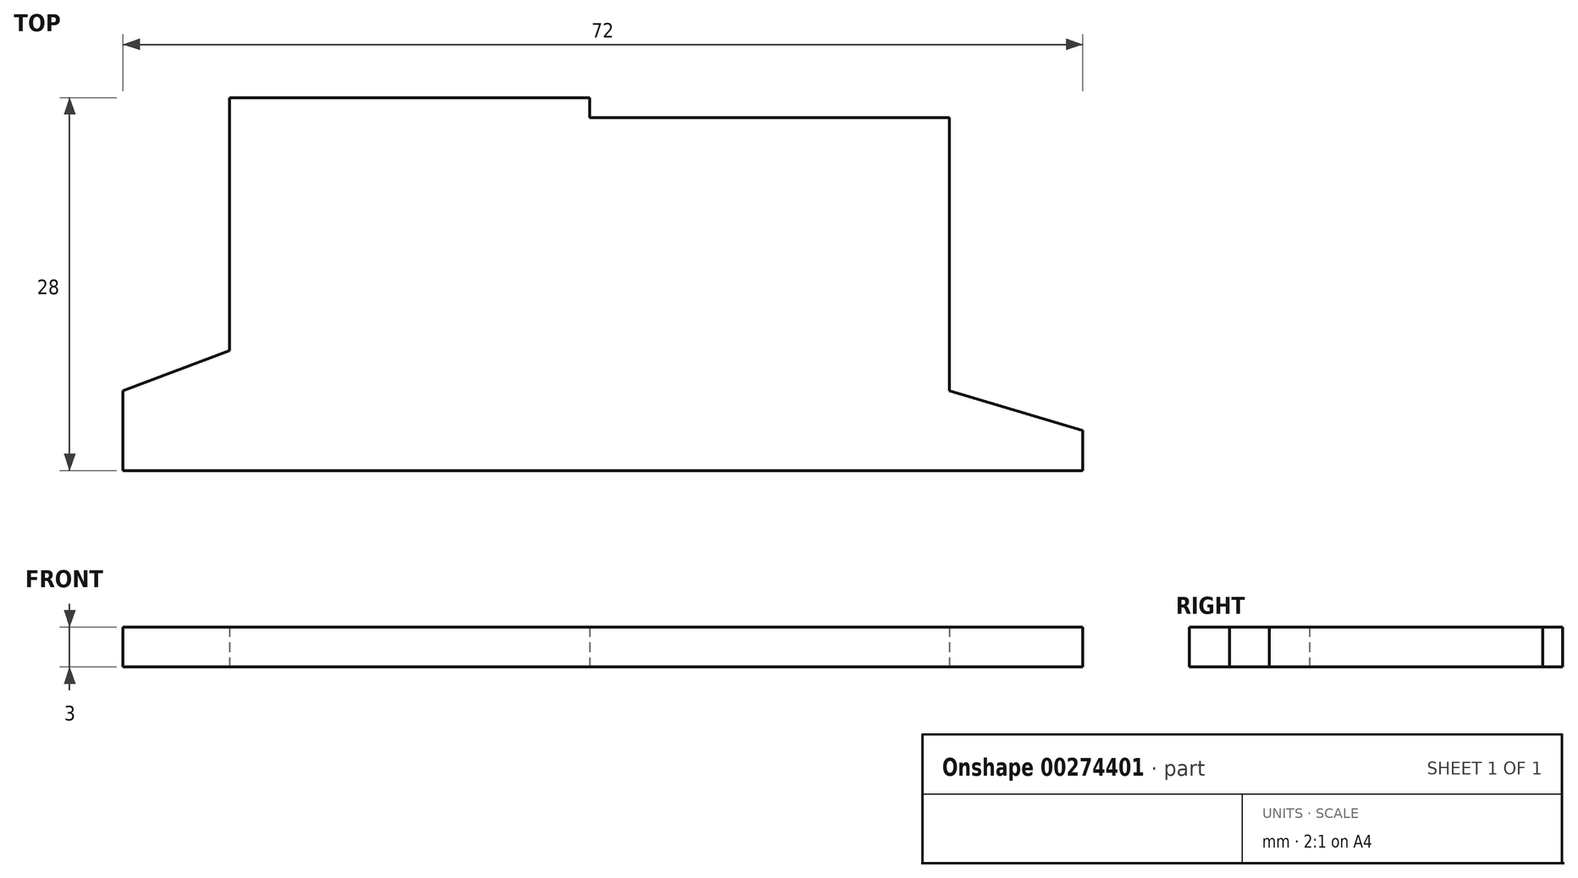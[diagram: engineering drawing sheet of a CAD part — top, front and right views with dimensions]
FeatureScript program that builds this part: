
annotation { "Feature Type Name" : "Feature", "Feature Type Description" : "" }
export const myFeature = defineFeature(function(context is Context, id is Id, definition is map)
    precondition{}
    {
        {
            var Q0;
            Q0=qCreatedBy(makeId("Top.planeOp"),FACE);
            var sketch = newSketch(context, id + "F0", { "sketchPlane" : qUnion([Q0])});
            skLineSegment(sketch, "E0.bottom", {"start": v(0, 0) * mm, "end": v(72, 0) * mm});
            skLineSegment(sketch, "E0.top", {"start": v(8, 28) * mm, "end": v(35, 28) * mm});
            skLineSegment(sketch, "E0.left", {"start": v(0, 0) * mm, "end": v(0, 6) * mm});
            skLineSegment(sketch, "E0.right", {"start": v(72, 0) * mm, "end": v(72, 3) * mm});
            skLineSegment(sketch, "E1", {"start": v(0, 0) * mm, "end": v(0, 6) * mm, "construction": true});
            skLineSegment(sketch, "E2", {"start": v(0, 6) * mm, "end": v(8, 6) * mm, "construction": true});
            skLineSegment(sketch, "E3", {"start": v(8, 6) * mm, "end": v(8, 9) * mm, "construction": true});
            skLineSegment(sketch, "E4", {"start": v(0, 6) * mm, "end": v(8, 9) * mm});
            skLineSegment(sketch, "E5", {"start": v(8, 28) * mm, "end": v(8, 9) * mm});
            skLineSegment(sketch, "E6", {"start": v(35, 28) * mm, "end": v(35, 26.5) * mm});
            skLineSegment(sketch, "E7", {"start": v(35, 26.5) * mm, "end": v(62, 26.5) * mm});
            skLineSegment(sketch, "E8", {"start": v(62, 26.5) * mm, "end": v(62, 6) * mm});
            skLineSegment(sketch, "E9", {"start": v(72, 3) * mm, "end": v(62, 6) * mm});
            skSolve(sketch);
        }
        {
            var Q0;
            Q0=makeQuery(id+"F0.imprint","IMPRINT",FACE,{"disambiguationData":[TD([[makeQuery(id+"F0.imprint","IMPRINT",EDGE,{"derivedFrom":sQuery(id+"F0.wireOp",EDGE,"E0.bottom")}),1.0]])]});
            extrude(context, id + "F1", {"entities" : qUnion([Q0]), "depth" : 3 * mm});
        }
    });
